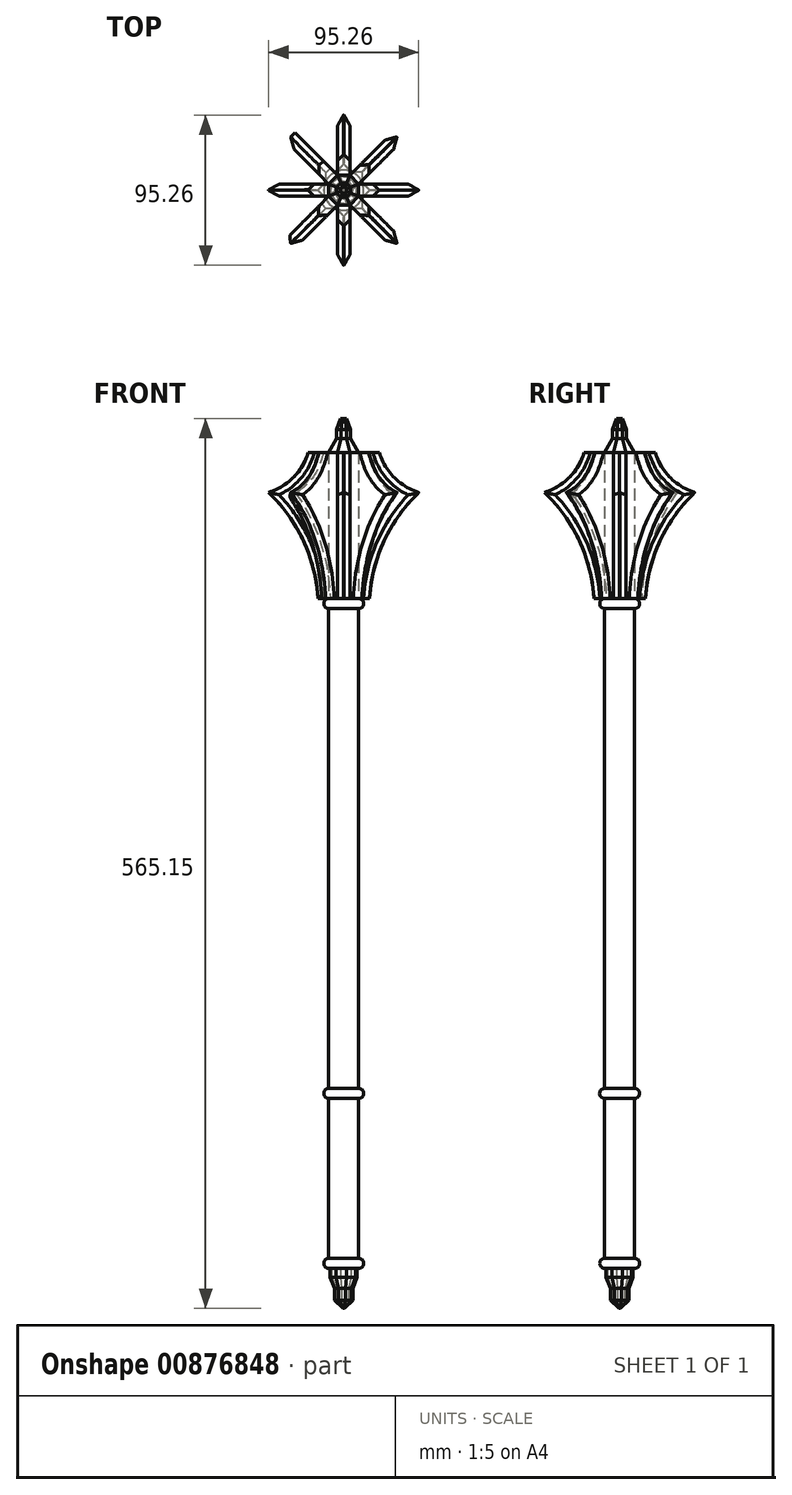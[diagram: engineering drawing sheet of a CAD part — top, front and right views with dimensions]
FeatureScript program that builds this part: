
annotation { "Feature Type Name" : "Feature", "Feature Type Description" : "" }
export const myFeature = defineFeature(function(context is Context, id is Id, definition is map)
    precondition{}
    {
        {
            var Q0;
            Q0=qCreatedBy(makeId("Top.planeOp"),FACE);
            var sketch = newSketch(context, id + "F0", { "sketchPlane" : qUnion([Q0])});
            skCircle(sketch, "E0", {"center": v(0, 0) * mm, "radius": 12.7 * mm});
            skSolve(sketch);
        }
        {
            var Q0;
            Q0 = qSketchRegion(id + "F0", true);
            extrude(context, id + "F1", {"entities" : qUnion([Q0]), "depth" : 6.35 * mm, "offsetDistance" : 25.4 * mm});
        }
        {
            var Q0;
            Q0=makeQuery(id+"F1.opExtrude","CAP_EDGE",EDGE,{"disambiguationData":[OSD([sQuery(id+"F0.wireOp",EDGE,"E0")])],"isStart":false});
            var Q1;
            Q1=makeQuery(id+"F1.opExtrude","CAP_EDGE",EDGE,{"disambiguationData":[OSD([sQuery(id+"F0.wireOp",EDGE,"E0")])],"isStart":true});
            fillet(context, id + "F2", {"entities" : qUnion([Q0, Q1]), "radius" : 3.17 * mm, "tangentPropagation" : true, "allowEdgeOverflow" : false});
        }
        {
            var Q0;
            Q0=makeQuery(id+"F1.opExtrude","CAP_FACE",FACE,{"disambiguationData":[OSD([sQuery(id+"F0.wireOp",EDGE,"E0")])],"isStart":false});
            extrude(context, id + "F3", {"entities" : qUnion([Q0]), "operationType" : NewBodyOperationType.ADD, "depth" : 101.6 * mm, "offsetDistance" : 25.4 * mm});
        }
        {
            var Q0;
            Q0=makeQuery(id+"F3.opExtrude","CAP_FACE",FACE,{"disambiguationData":[OSD([sQuery(id+"F0.wireOp",EDGE,"E0")])],"isStart":false});
            var sketch = newSketch(context, id + "F4", { "sketchPlane" : qUnion([Q0])});
            skCircle(sketch, "E1", {"center": v(0, 0) * mm, "radius": 12.7 * mm});
            skSolve(sketch);
        }
        {
            var Q0;
            Q0 = qSketchRegion(id + "F4", true);
            extrude(context, id + "F5", {"entities" : qUnion([Q0]), "operationType" : NewBodyOperationType.ADD, "depth" : 6.35 * mm, "offsetDistance" : 25.4 * mm});
        }
        {
            var Q0;
            Q0=makeQuery(id+"F5.opExtrude","CAP_EDGE",EDGE,{"disambiguationData":[OSD([sQuery(id+"F4.wireOp",EDGE,"E1")])],"isStart":false});
            var Q1;
            Q1=makeQuery(id+"F5.opExtrude","CAP_EDGE",EDGE,{"disambiguationData":[OSD([sQuery(id+"F4.wireOp",EDGE,"E1")])],"isStart":true});
            fillet(context, id + "F6", {"entities" : qUnion([Q0, Q1]), "radius" : 3.17 * mm, "tangentPropagation" : true, "allowEdgeOverflow" : false});
        }
        {
            var Q0;
            Q0=makeQuery(id+"F1.opExtrude","CAP_FACE",FACE,{"disambiguationData":[OSD([sQuery(id+"F0.wireOp",EDGE,"E0")])],"isStart":true});
            var sketch = newSketch(context, id + "F7", { "sketchPlane" : qUnion([Q0])});
            skCircle(sketch, "E2", {"center": v(0, 0) * mm, "radius": 6.35 * mm});
            skSolve(sketch);
        }
        {
            var Q0;
            Q0=makeQuery(id+"F5.opExtrude","CAP_FACE",FACE,{"disambiguationData":[OSD([sQuery(id+"F4.wireOp",EDGE,"E1")])],"isStart":false});
            extrude(context, id + "F8", {"entities" : qUnion([Q0]), "operationType" : NewBodyOperationType.ADD, "depth" : 304.8 * mm, "offsetDistance" : 25.4 * mm});
        }
        {
            var Q0;
            Q0=makeQuery(id+"F8.opExtrude","CAP_FACE",FACE,{"disambiguationData":[OSD([sQuery(id+"F4.wireOp",EDGE,"E1")])],"isStart":false});
            var sketch = newSketch(context, id + "F9", { "sketchPlane" : qUnion([Q0])});
            skCircle(sketch, "E3", {"center": v(0, 0) * mm, "radius": 12.7 * mm});
            skSolve(sketch);
        }
        {
            var Q0;
            Q0 = qSketchRegion(id + "F9", true);
            extrude(context, id + "F10", {"entities" : qUnion([Q0]), "operationType" : NewBodyOperationType.ADD, "depth" : 6.35 * mm, "offsetDistance" : 25.4 * mm});
        }
        {
            var Q0;
            Q0=makeQuery(id+"F10.opExtrude","CAP_EDGE",EDGE,{"disambiguationData":[OSD([sQuery(id+"F9.wireOp",EDGE,"E3")])],"isStart":false});
            var Q1;
            Q1=makeQuery(id+"F10.opExtrude","CAP_EDGE",EDGE,{"disambiguationData":[OSD([sQuery(id+"F9.wireOp",EDGE,"E3")])],"isStart":true});
            fillet(context, id + "F11", {"entities" : qUnion([Q0, Q1]), "radius" : 3.17 * mm, "tangentPropagation" : true, "allowEdgeOverflow" : false});
        }
        {
            var Q0;
            Q0=makeQuery(id+"F10.opExtrude","CAP_FACE",FACE,{"disambiguationData":[OSD([sQuery(id+"F9.wireOp",EDGE,"E3")])],"isStart":false});
            var sketch = newSketch(context, id + "F12", { "sketchPlane" : qUnion([Q0])});
            skCircle(sketch, "E4.cCircle", {"center": v(0, 0) * mm, "radius": 9.53 * mm, "construction": true});
            skLineSegment(sketch, "E4.0", {"start": v(-3.95, 9.53) * mm, "end": v(3.95, 9.53) * mm});
            skLineSegment(sketch, "E4.1", {"start": v(3.95, 9.53) * mm, "end": v(9.53, 3.95) * mm});
            skLineSegment(sketch, "E4.2", {"start": v(9.53, 3.95) * mm, "end": v(9.53, -3.95) * mm});
            skLineSegment(sketch, "E4.3", {"start": v(9.53, -3.95) * mm, "end": v(3.95, -9.53) * mm});
            skLineSegment(sketch, "E4.4", {"start": v(3.95, -9.53) * mm, "end": v(-3.95, -9.53) * mm});
            skLineSegment(sketch, "E4.5", {"start": v(-3.95, -9.53) * mm, "end": v(-9.52, -3.95) * mm});
            skLineSegment(sketch, "E4.6", {"start": v(-9.52, -3.95) * mm, "end": v(-9.53, 3.95) * mm});
            skLineSegment(sketch, "E4.7", {"start": v(-9.53, 3.95) * mm, "end": v(-3.95, 9.53) * mm});
            skPoint(sketch, "E4.0.midPoint", {"position": v(0, 9.53) * mm});
            skSolve(sketch);
        }
        {
            var Q0;
            Q0 = qSketchRegion(id + "F12", true);
            extrude(context, id + "F13", {"entities" : qUnion([Q0]), "operationType" : NewBodyOperationType.ADD, "depth" : 101.6 * mm, "offsetDistance" : 25.4 * mm});
        }
        {
            var Q0;
            Q0=makeQuery(id+"F13.opExtrude","CAP_EDGE",EDGE,{"disambiguationData":[OSD([sQuery(id+"F12.wireOp",EDGE,"E4.5")])],"isStart":false});
            var Q1;
            Q1=makeQuery(id+"F13.opExtrude","CAP_EDGE",EDGE,{"disambiguationData":[OSD([sQuery(id+"F12.wireOp",EDGE,"E4.6")])],"isStart":false});
            var Q2;
            Q2=makeQuery(id+"F13.opExtrude","CAP_EDGE",EDGE,{"disambiguationData":[OSD([sQuery(id+"F12.wireOp",EDGE,"E4.0")])],"isStart":false});
            var Q3;
            Q3=makeQuery(id+"F13.opExtrude","CAP_EDGE",EDGE,{"disambiguationData":[OSD([sQuery(id+"F12.wireOp",EDGE,"E4.1")])],"isStart":false});
            var Q4;
            Q4=makeQuery(id+"F13.opExtrude","CAP_EDGE",EDGE,{"disambiguationData":[OSD([sQuery(id+"F12.wireOp",EDGE,"E4.2")])],"isStart":false});
            var Q5;
            Q5=makeQuery(id+"F13.opExtrude","CAP_EDGE",EDGE,{"disambiguationData":[OSD([sQuery(id+"F12.wireOp",EDGE,"E4.4")])],"isStart":false});
            var Q6;
            Q6=makeQuery(id+"F13.opExtrude","CAP_EDGE",EDGE,{"disambiguationData":[OSD([sQuery(id+"F12.wireOp",EDGE,"E4.7")])],"isStart":false});
            var Q7;
            Q7=makeQuery(id+"F13.opExtrude","CAP_EDGE",EDGE,{"disambiguationData":[OSD([sQuery(id+"F12.wireOp",EDGE,"E4.3")])],"isStart":false});
            chamfer(context, id + "F14", {"entities" : qUnion([Q0, Q1, Q2, Q3, Q4, Q5, Q6, Q7]), "chamferType" : ChamferType.OFFSET_ANGLE, "width" : 5.08 * mm, "oppositeDirection" : true, "angle" : 60 * degree, "tangentPropagation" : true});
        }
        {
            var Q0;
            Q0=makeQuery(id+"F13.opExtrude","SWEPT_FACE",FACE,{"disambiguationData":[OSD([sQuery(id+"F12.wireOp",EDGE,"E4.6")])]});
            extrude(context, id + "F15", {"entities" : qUnion([Q0]), "operationType" : NewBodyOperationType.ADD, "depth" : 38.1 * mm, "offsetDistance" : 25.4 * mm});
        }
        {
            var Q0;
            Q0=makeQuery(id+"F13.opExtrude","SWEPT_FACE",FACE,{"disambiguationData":[OSD([sQuery(id+"F12.wireOp",EDGE,"E4.5")])]});
            extrude(context, id + "F16", {"entities" : qUnion([Q0]), "operationType" : NewBodyOperationType.ADD, "depth" : 38.1 * mm, "offsetDistance" : 25.4 * mm});
        }
        {
            var Q0;
            Q0=makeQuery(id+"F13.opExtrude","SWEPT_FACE",FACE,{"disambiguationData":[OSD([sQuery(id+"F12.wireOp",EDGE,"E4.4")])]});
            extrude(context, id + "F17", {"entities" : qUnion([Q0]), "operationType" : NewBodyOperationType.ADD, "depth" : 38.1 * mm, "offsetDistance" : 25.4 * mm});
        }
        {
            var Q0;
            Q0=makeQuery(id+"F13.opExtrude","SWEPT_FACE",FACE,{"disambiguationData":[OSD([sQuery(id+"F12.wireOp",EDGE,"E4.7")])]});
            extrude(context, id + "F18", {"entities" : qUnion([Q0]), "operationType" : NewBodyOperationType.ADD, "depth" : 38.1 * mm, "offsetDistance" : 25.4 * mm});
        }
        {
            var Q0;
            Q0=makeQuery(id+"F13.opExtrude","SWEPT_FACE",FACE,{"disambiguationData":[OSD([sQuery(id+"F12.wireOp",EDGE,"E4.0")])]});
            extrude(context, id + "F19", {"entities" : qUnion([Q0]), "operationType" : NewBodyOperationType.ADD, "depth" : 38.1 * mm, "offsetDistance" : 25.4 * mm});
        }
        {
            var Q0;
            Q0=makeQuery(id+"F13.opExtrude","SWEPT_FACE",FACE,{"disambiguationData":[OSD([sQuery(id+"F12.wireOp",EDGE,"E4.1")])]});
            extrude(context, id + "F20", {"entities" : qUnion([Q0]), "operationType" : NewBodyOperationType.ADD, "depth" : 38.1 * mm, "offsetDistance" : 25.4 * mm});
        }
        {
            var Q0;
            Q0=makeQuery(id+"F13.opExtrude","SWEPT_FACE",FACE,{"disambiguationData":[OSD([sQuery(id+"F12.wireOp",EDGE,"E4.2")])]});
            extrude(context, id + "F21", {"entities" : qUnion([Q0]), "operationType" : NewBodyOperationType.ADD, "depth" : 38.1 * mm, "offsetDistance" : 25.4 * mm});
        }
        {
            var Q0;
            Q0=makeQuery(id+"F13.opExtrude","SWEPT_FACE",FACE,{"disambiguationData":[OSD([sQuery(id+"F12.wireOp",EDGE,"E4.3")])]});
            extrude(context, id + "F22", {"entities" : qUnion([Q0]), "operationType" : NewBodyOperationType.ADD, "depth" : 38.1 * mm, "offsetDistance" : 25.4 * mm});
        }
        {
            var Q0;
            Q0=makeQuery(id+"F18.opExtrude","SWEPT_FACE",FACE,{"disambiguationData":[OSD([sQuery(id+"F12.wireOp",EDGE,"E4.0"),sQuery(id+"F12.wireOp",EDGE,"E4.7")])]});
            var sketch = newSketch(context, id + "F23", { "sketchPlane" : qUnion([Q0])});
            skLineSegment(sketch, "E5", {"start": v(9.53, 518.25) * mm, "end": v(22.23, 518.25) * mm});
            skLineSegment(sketch, "E6", {"start": v(9.53, 425.45) * mm, "end": v(15.88, 425.45) * mm});
            skLineSegment(sketch, "E7", {"start": v(47.62, 518.25) * mm, "end": v(47.62, 425.45) * mm});
            skLineSegment(sketch, "E8", {"start": v(47.62, 518.25) * mm, "end": v(47.62, 467.45) * mm});
            skLineSegment(sketch, "E9", {"start": v(47.62, 518.25) * mm, "end": v(47.62, 492.85) * mm});
            skArc(sketch, "E10", {"start": v(22.23, 518.25) * mm, "mid": v(31.74, 502.37) * mm, "end": v(47.62, 492.85) * mm});
            skArc(sketch, "E11", {"start": v(47.62, 492.85) * mm, "mid": v(25.35, 462.17) * mm, "end": v(15.87, 425.45) * mm});
            skSolve(sketch);
        }
        {
            var Q0;
            {var subQ0=sQuery(id+"F23.wireOp",EDGE,"E8");Q0=makeQuery(id+"F23.imprint","IMPRINT",FACE,{"disambiguationData":[TD([[makeQuery(id+"F23.imprint","IMPRINT",EDGE,{"derivedFrom":subQ0}),-1.0]])]});}
            var Q1;
            {var subQ0=sQuery(id+"F23.wireOp",EDGE,"E7");Q1=makeQuery(id+"F23.imprint","IMPRINT",FACE,{"disambiguationData":[TD([[makeQuery(id+"F23.imprint","IMPRINT",EDGE,{"derivedFrom":subQ0}),-1.0]])]});}
            var Q2;
            {var subQ0=sQuery(id+"F23.wireOp",EDGE,"E9");Q2=makeQuery(id+"F23.imprint","IMPRINT",FACE,{"disambiguationData":[TD([[makeQuery(id+"F23.imprint","IMPRINT",EDGE,{"derivedFrom":subQ0}),-1.0]])]});}
            extrude(context, id + "F24", {"entities" : qUnion([Q0, Q1, Q2]), "operationType" : NewBodyOperationType.REMOVE, "oppositeDirection" : true, "depth" : 12.7 * mm, "offsetDistance" : 25.4 * mm});
        }
        {
            var Q0;
            Q0=makeQuery(id+"F13.opExtrude","CAP_FACE",FACE,{"disambiguationData":[OSD([sQuery(id+"F12.wireOp",EDGE,"E4.0"),sQuery(id+"F12.wireOp",EDGE,"E4.1"),sQuery(id+"F12.wireOp",EDGE,"E4.2"),sQuery(id+"F12.wireOp",EDGE,"E4.3"),sQuery(id+"F12.wireOp",EDGE,"E4.4"),sQuery(id+"F12.wireOp",EDGE,"E4.5"),sQuery(id+"F12.wireOp",EDGE,"E4.6"),sQuery(id+"F12.wireOp",EDGE,"E4.7")])],"isStart":false});
            extrude(context, id + "F25", {"entities" : qUnion([Q0]), "operationType" : NewBodyOperationType.ADD, "depth" : 12.7 * mm, "offsetDistance" : 25.4 * mm});
        }
        {
            var Q0;
            {var subQ0=sQuery(id+"F12.wireOp",EDGE,"E4.7");var subQ1=sQuery(id+"F12.wireOp",EDGE,"E4.6");var subQ2=sQuery(id+"F12.wireOp",EDGE,"E4.5");var subQ3=sQuery(id+"F12.wireOp",EDGE,"E4.4");var subQ4=sQuery(id+"F12.wireOp",EDGE,"E4.3");var subQ5=sQuery(id+"F12.wireOp",EDGE,"E4.2");var subQ6=sQuery(id+"F12.wireOp",EDGE,"E4.1");var subQ7=sQuery(id+"F12.wireOp",EDGE,"E4.0");Q0=makeQuery(id+"F25.opExtrude","CAP_EDGE",EDGE,{"disambiguationData":[OSD([subQ7,subQ6,subQ5,subQ4,subQ3,subQ2,subQ1,subQ0]),TDD([makeQuery(id+"F14.opChamfer","BLEND_EDGE",EDGE,{"blendedFrom":[makeQuery(id+"F13.opExtrude","CAP_EDGE",EDGE,{"disambiguationData":[OSD([subQ0])],"isStart":false}),makeQuery(id+"F13.opExtrude","CAP_FACE",FACE,{"disambiguationData":[OSD([subQ7,subQ6,subQ5,subQ4,subQ3,subQ2,subQ1,subQ0])],"isStart":false})],"blendedInto":[makeQuery(id+"F13.opExtrude","CAP_FACE",FACE,{"disambiguationData":[OSD([subQ7,subQ6,subQ5,subQ4,subQ3,subQ2,subQ1,subQ0])],"isStart":false})]})])],"isStart":false});}
            var Q1;
            {var subQ0=sQuery(id+"F12.wireOp",EDGE,"E4.7");var subQ1=sQuery(id+"F12.wireOp",EDGE,"E4.6");var subQ2=sQuery(id+"F12.wireOp",EDGE,"E4.5");var subQ3=sQuery(id+"F12.wireOp",EDGE,"E4.4");var subQ4=sQuery(id+"F12.wireOp",EDGE,"E4.3");var subQ5=sQuery(id+"F12.wireOp",EDGE,"E4.2");var subQ6=sQuery(id+"F12.wireOp",EDGE,"E4.1");var subQ7=sQuery(id+"F12.wireOp",EDGE,"E4.0");Q1=makeQuery(id+"F25.opExtrude","CAP_EDGE",EDGE,{"disambiguationData":[OSD([subQ7,subQ6,subQ5,subQ4,subQ3,subQ2,subQ1,subQ0]),TDD([makeQuery(id+"F14.opChamfer","BLEND_EDGE",EDGE,{"blendedFrom":[makeQuery(id+"F13.opExtrude","CAP_EDGE",EDGE,{"disambiguationData":[OSD([subQ7])],"isStart":false}),makeQuery(id+"F13.opExtrude","CAP_FACE",FACE,{"disambiguationData":[OSD([subQ7,subQ6,subQ5,subQ4,subQ3,subQ2,subQ1,subQ0])],"isStart":false})],"blendedInto":[makeQuery(id+"F13.opExtrude","CAP_FACE",FACE,{"disambiguationData":[OSD([subQ7,subQ6,subQ5,subQ4,subQ3,subQ2,subQ1,subQ0])],"isStart":false})]})])],"isStart":false});}
            var Q2;
            {var subQ0=sQuery(id+"F12.wireOp",EDGE,"E4.7");var subQ1=sQuery(id+"F12.wireOp",EDGE,"E4.6");var subQ2=sQuery(id+"F12.wireOp",EDGE,"E4.5");var subQ3=sQuery(id+"F12.wireOp",EDGE,"E4.4");var subQ4=sQuery(id+"F12.wireOp",EDGE,"E4.3");var subQ5=sQuery(id+"F12.wireOp",EDGE,"E4.2");var subQ6=sQuery(id+"F12.wireOp",EDGE,"E4.1");var subQ7=sQuery(id+"F12.wireOp",EDGE,"E4.0");Q2=makeQuery(id+"F25.opExtrude","CAP_EDGE",EDGE,{"disambiguationData":[OSD([subQ7,subQ6,subQ5,subQ4,subQ3,subQ2,subQ1,subQ0]),TDD([makeQuery(id+"F14.opChamfer","BLEND_EDGE",EDGE,{"blendedFrom":[makeQuery(id+"F13.opExtrude","CAP_EDGE",EDGE,{"disambiguationData":[OSD([subQ6])],"isStart":false}),makeQuery(id+"F13.opExtrude","CAP_FACE",FACE,{"disambiguationData":[OSD([subQ7,subQ6,subQ5,subQ4,subQ3,subQ2,subQ1,subQ0])],"isStart":false})],"blendedInto":[makeQuery(id+"F13.opExtrude","CAP_FACE",FACE,{"disambiguationData":[OSD([subQ7,subQ6,subQ5,subQ4,subQ3,subQ2,subQ1,subQ0])],"isStart":false})]})])],"isStart":false});}
            var Q3;
            {var subQ0=sQuery(id+"F12.wireOp",EDGE,"E4.7");var subQ1=sQuery(id+"F12.wireOp",EDGE,"E4.6");var subQ2=sQuery(id+"F12.wireOp",EDGE,"E4.5");var subQ3=sQuery(id+"F12.wireOp",EDGE,"E4.4");var subQ4=sQuery(id+"F12.wireOp",EDGE,"E4.3");var subQ5=sQuery(id+"F12.wireOp",EDGE,"E4.2");var subQ6=sQuery(id+"F12.wireOp",EDGE,"E4.1");var subQ7=sQuery(id+"F12.wireOp",EDGE,"E4.0");Q3=makeQuery(id+"F25.opExtrude","CAP_EDGE",EDGE,{"disambiguationData":[OSD([subQ7,subQ6,subQ5,subQ4,subQ3,subQ2,subQ1,subQ0]),TDD([makeQuery(id+"F14.opChamfer","BLEND_EDGE",EDGE,{"blendedFrom":[makeQuery(id+"F13.opExtrude","CAP_EDGE",EDGE,{"disambiguationData":[OSD([subQ5])],"isStart":false}),makeQuery(id+"F13.opExtrude","CAP_FACE",FACE,{"disambiguationData":[OSD([subQ7,subQ6,subQ5,subQ4,subQ3,subQ2,subQ1,subQ0])],"isStart":false})],"blendedInto":[makeQuery(id+"F13.opExtrude","CAP_FACE",FACE,{"disambiguationData":[OSD([subQ7,subQ6,subQ5,subQ4,subQ3,subQ2,subQ1,subQ0])],"isStart":false})]})])],"isStart":false});}
            var Q4;
            {var subQ0=sQuery(id+"F12.wireOp",EDGE,"E4.7");var subQ1=sQuery(id+"F12.wireOp",EDGE,"E4.6");var subQ2=sQuery(id+"F12.wireOp",EDGE,"E4.5");var subQ3=sQuery(id+"F12.wireOp",EDGE,"E4.4");var subQ4=sQuery(id+"F12.wireOp",EDGE,"E4.3");var subQ5=sQuery(id+"F12.wireOp",EDGE,"E4.2");var subQ6=sQuery(id+"F12.wireOp",EDGE,"E4.1");var subQ7=sQuery(id+"F12.wireOp",EDGE,"E4.0");Q4=makeQuery(id+"F25.opExtrude","CAP_EDGE",EDGE,{"disambiguationData":[OSD([subQ7,subQ6,subQ5,subQ4,subQ3,subQ2,subQ1,subQ0]),TDD([makeQuery(id+"F14.opChamfer","BLEND_EDGE",EDGE,{"blendedFrom":[makeQuery(id+"F13.opExtrude","CAP_EDGE",EDGE,{"disambiguationData":[OSD([subQ4])],"isStart":false}),makeQuery(id+"F13.opExtrude","CAP_FACE",FACE,{"disambiguationData":[OSD([subQ7,subQ6,subQ5,subQ4,subQ3,subQ2,subQ1,subQ0])],"isStart":false})],"blendedInto":[makeQuery(id+"F13.opExtrude","CAP_FACE",FACE,{"disambiguationData":[OSD([subQ7,subQ6,subQ5,subQ4,subQ3,subQ2,subQ1,subQ0])],"isStart":false})]})])],"isStart":false});}
            var Q5;
            {var subQ0=sQuery(id+"F12.wireOp",EDGE,"E4.7");var subQ1=sQuery(id+"F12.wireOp",EDGE,"E4.6");var subQ2=sQuery(id+"F12.wireOp",EDGE,"E4.5");var subQ3=sQuery(id+"F12.wireOp",EDGE,"E4.4");var subQ4=sQuery(id+"F12.wireOp",EDGE,"E4.3");var subQ5=sQuery(id+"F12.wireOp",EDGE,"E4.2");var subQ6=sQuery(id+"F12.wireOp",EDGE,"E4.1");var subQ7=sQuery(id+"F12.wireOp",EDGE,"E4.0");Q5=makeQuery(id+"F25.opExtrude","CAP_EDGE",EDGE,{"disambiguationData":[OSD([subQ7,subQ6,subQ5,subQ4,subQ3,subQ2,subQ1,subQ0]),TDD([makeQuery(id+"F14.opChamfer","BLEND_EDGE",EDGE,{"blendedFrom":[makeQuery(id+"F13.opExtrude","CAP_EDGE",EDGE,{"disambiguationData":[OSD([subQ3])],"isStart":false}),makeQuery(id+"F13.opExtrude","CAP_FACE",FACE,{"disambiguationData":[OSD([subQ7,subQ6,subQ5,subQ4,subQ3,subQ2,subQ1,subQ0])],"isStart":false})],"blendedInto":[makeQuery(id+"F13.opExtrude","CAP_FACE",FACE,{"disambiguationData":[OSD([subQ7,subQ6,subQ5,subQ4,subQ3,subQ2,subQ1,subQ0])],"isStart":false})]})])],"isStart":false});}
            var Q6;
            {var subQ0=sQuery(id+"F12.wireOp",EDGE,"E4.7");var subQ1=sQuery(id+"F12.wireOp",EDGE,"E4.6");var subQ2=sQuery(id+"F12.wireOp",EDGE,"E4.5");var subQ3=sQuery(id+"F12.wireOp",EDGE,"E4.4");var subQ4=sQuery(id+"F12.wireOp",EDGE,"E4.3");var subQ5=sQuery(id+"F12.wireOp",EDGE,"E4.2");var subQ6=sQuery(id+"F12.wireOp",EDGE,"E4.1");var subQ7=sQuery(id+"F12.wireOp",EDGE,"E4.0");Q6=makeQuery(id+"F25.opExtrude","CAP_EDGE",EDGE,{"disambiguationData":[OSD([subQ7,subQ6,subQ5,subQ4,subQ3,subQ2,subQ1,subQ0]),TDD([makeQuery(id+"F14.opChamfer","BLEND_EDGE",EDGE,{"blendedFrom":[makeQuery(id+"F13.opExtrude","CAP_EDGE",EDGE,{"disambiguationData":[OSD([subQ2])],"isStart":false}),makeQuery(id+"F13.opExtrude","CAP_FACE",FACE,{"disambiguationData":[OSD([subQ7,subQ6,subQ5,subQ4,subQ3,subQ2,subQ1,subQ0])],"isStart":false})],"blendedInto":[makeQuery(id+"F13.opExtrude","CAP_FACE",FACE,{"disambiguationData":[OSD([subQ7,subQ6,subQ5,subQ4,subQ3,subQ2,subQ1,subQ0])],"isStart":false})]})])],"isStart":false});}
            var Q7;
            {var subQ0=sQuery(id+"F12.wireOp",EDGE,"E4.7");var subQ1=sQuery(id+"F12.wireOp",EDGE,"E4.6");var subQ2=sQuery(id+"F12.wireOp",EDGE,"E4.5");var subQ3=sQuery(id+"F12.wireOp",EDGE,"E4.4");var subQ4=sQuery(id+"F12.wireOp",EDGE,"E4.3");var subQ5=sQuery(id+"F12.wireOp",EDGE,"E4.2");var subQ6=sQuery(id+"F12.wireOp",EDGE,"E4.1");var subQ7=sQuery(id+"F12.wireOp",EDGE,"E4.0");Q7=makeQuery(id+"F25.opExtrude","CAP_EDGE",EDGE,{"disambiguationData":[OSD([subQ7,subQ6,subQ5,subQ4,subQ3,subQ2,subQ1,subQ0]),TDD([makeQuery(id+"F14.opChamfer","BLEND_EDGE",EDGE,{"blendedFrom":[makeQuery(id+"F13.opExtrude","CAP_EDGE",EDGE,{"disambiguationData":[OSD([subQ1])],"isStart":false}),makeQuery(id+"F13.opExtrude","CAP_FACE",FACE,{"disambiguationData":[OSD([subQ7,subQ6,subQ5,subQ4,subQ3,subQ2,subQ1,subQ0])],"isStart":false})],"blendedInto":[makeQuery(id+"F13.opExtrude","CAP_FACE",FACE,{"disambiguationData":[OSD([subQ7,subQ6,subQ5,subQ4,subQ3,subQ2,subQ1,subQ0])],"isStart":false})]})])],"isStart":false});}
            chamfer(context, id + "F26", {"entities" : qUnion([Q0, Q1, Q2, Q3, Q4, Q5, Q6, Q7]), "chamferType" : ChamferType.OFFSET_ANGLE, "width" : 2.54 * mm, "oppositeDirection" : false, "angle" : 70 * degree, "tangentPropagation" : true});
        }
        {
            var Q0;
            {var subQ0=sQuery(id+"F23.wireOp",EDGE,"E9");Q0=makeQuery(id+"F23.imprint","IMPRINT",FACE,{"disambiguationData":[TD([[makeQuery(id+"F23.imprint","IMPRINT",EDGE,{"derivedFrom":subQ0}),-1.0]])]});}
            var Q1;
            {var subQ0=sQuery(id+"F23.wireOp",EDGE,"E7");Q1=makeQuery(id+"F23.imprint","IMPRINT",FACE,{"disambiguationData":[TD([[makeQuery(id+"F23.imprint","IMPRINT",EDGE,{"derivedFrom":subQ0}),-1.0]])]});}
            var Q2;
            {var subQ0=sQuery(id+"F0.wireOp",EDGE,"E0");Q2=makeQuery(id+"F2.opFillet","BLEND_EDGE",EDGE,{"blendedFrom":[makeQuery(id+"F1.opExtrude","CAP_EDGE",EDGE,{"disambiguationData":[OSD([subQ0])],"isStart":true}),makeQuery(id+"F1.opExtrude","CAP_FACE",FACE,{"disambiguationData":[OSD([subQ0])],"isStart":true})],"blendedInto":[makeQuery(id+"F1.opExtrude","CAP_FACE",FACE,{"disambiguationData":[OSD([subQ0])],"isStart":true})]});}
            revolve(context, id + "F27", {"operationType" : NewBodyOperationType.REMOVE, "surfaceOperationType" : NewSurfaceOperationType.NEW, "entities" : qUnion([Q0, Q1]), "axis" : qUnion([Q2]), "revolveType" : RevolveType.FULL, "oppositeDirection" : true});
        }
        {
            var Q0;
            Q0=makeQuery(id+"F7.imprint","IMPRINT",FACE,{"disambiguationData":[TD([[makeQuery(id+"F7.imprint","IMPRINT",EDGE,{"derivedFrom":sQuery(id+"F7.wireOp",EDGE,"E2")}),-1.0]])]});
            var sketch = newSketch(context, id + "F28", { "sketchPlane" : qUnion([Q0])});
            skCircle(sketch, "E12.cCircle", {"center": v(0, 0) * mm, "radius": 8.09 * mm, "construction": true});
            skLineSegment(sketch, "E12.0", {"start": v(-7.31, -4.8) * mm, "end": v(-8.57, 1.77) * mm});
            skLineSegment(sketch, "E12.1", {"start": v(-8.57, 1.77) * mm, "end": v(-4.8, 7.31) * mm});
            skLineSegment(sketch, "E12.2", {"start": v(-4.8, 7.31) * mm, "end": v(1.77, 8.57) * mm});
            skLineSegment(sketch, "E12.3", {"start": v(1.77, 8.57) * mm, "end": v(7.31, 4.8) * mm});
            skLineSegment(sketch, "E12.4", {"start": v(7.31, 4.8) * mm, "end": v(8.57, -1.77) * mm});
            skLineSegment(sketch, "E12.5", {"start": v(8.57, -1.77) * mm, "end": v(4.8, -7.31) * mm});
            skLineSegment(sketch, "E12.6", {"start": v(4.8, -7.31) * mm, "end": v(-1.77, -8.57) * mm});
            skLineSegment(sketch, "E12.7", {"start": v(-1.77, -8.57) * mm, "end": v(-7.31, -4.8) * mm});
            skPoint(sketch, "E12.0.midPoint", {"position": v(-7.94, -1.52) * mm});
            skSolve(sketch);
        }
        {
            var Q0;
            Q0 = qSketchRegion(id + "F28", true);
            extrude(context, id + "F29", {"entities" : qUnion([Q0]), "operationType" : NewBodyOperationType.ADD, "depth" : 12.7 * mm, "offsetDistance" : 25.4 * mm});
        }
        {
            var Q0;
            Q0=makeQuery(id+"F29.opExtrude","CAP_EDGE",EDGE,{"disambiguationData":[OSD([sQuery(id+"F28.wireOp",EDGE,"E12.3")])],"isStart":false});
            var Q1;
            Q1=makeQuery(id+"F29.opExtrude","CAP_EDGE",EDGE,{"disambiguationData":[OSD([sQuery(id+"F28.wireOp",EDGE,"E12.4")])],"isStart":false});
            var Q2;
            Q2=makeQuery(id+"F29.opExtrude","CAP_FACE",FACE,{"disambiguationData":[OSD([sQuery(id+"F28.wireOp",EDGE,"E12.0"),sQuery(id+"F28.wireOp",EDGE,"E12.1"),sQuery(id+"F28.wireOp",EDGE,"E12.2"),sQuery(id+"F28.wireOp",EDGE,"E12.3"),sQuery(id+"F28.wireOp",EDGE,"E12.4"),sQuery(id+"F28.wireOp",EDGE,"E12.5"),sQuery(id+"F28.wireOp",EDGE,"E12.6"),sQuery(id+"F28.wireOp",EDGE,"E12.7")])],"isStart":false});
            chamfer(context, id + "F30", {"entities" : qUnion([Q0, Q1, Q2]), "chamferType" : ChamferType.OFFSET_ANGLE, "width" : 2.54 * mm, "oppositeDirection" : true, "angle" : 70 * degree, "tangentPropagation" : true});
        }
        {
            var Q0;
            Q0=makeQuery(id+"F29.opExtrude","CAP_FACE",FACE,{"disambiguationData":[OSD([sQuery(id+"F28.wireOp",EDGE,"E12.0"),sQuery(id+"F28.wireOp",EDGE,"E12.1"),sQuery(id+"F28.wireOp",EDGE,"E12.2"),sQuery(id+"F28.wireOp",EDGE,"E12.3"),sQuery(id+"F28.wireOp",EDGE,"E12.4"),sQuery(id+"F28.wireOp",EDGE,"E12.5"),sQuery(id+"F28.wireOp",EDGE,"E12.6"),sQuery(id+"F28.wireOp",EDGE,"E12.7")])],"isStart":false});
            extrude(context, id + "F31", {"entities" : qUnion([Q0]), "operationType" : NewBodyOperationType.ADD, "depth" : 12.7 * mm, "offsetDistance" : 25.4 * mm});
        }
        {
            var Q0;
            Q0=makeQuery(id+"F31.opExtrude","CAP_FACE",FACE,{"disambiguationData":[OSD([sQuery(id+"F28.wireOp",EDGE,"E12.0"),sQuery(id+"F28.wireOp",EDGE,"E12.1"),sQuery(id+"F28.wireOp",EDGE,"E12.2"),sQuery(id+"F28.wireOp",EDGE,"E12.3"),sQuery(id+"F28.wireOp",EDGE,"E12.4"),sQuery(id+"F28.wireOp",EDGE,"E12.5"),sQuery(id+"F28.wireOp",EDGE,"E12.6"),sQuery(id+"F28.wireOp",EDGE,"E12.7")])],"isStart":false});
            chamfer(context, id + "F32", {"entities" : qUnion([Q0]), "width" : 5.08 * mm, "tangentPropagation" : true});
        }
        {
            var Q0;
            Q0=makeQuery(id+"F27.boolean.opBoolean","INTERSECT",EDGE,{"derivedFrom":[makeQuery(id+"F16.opExtrude","SWEPT_FACE",FACE,{"disambiguationData":[OSD([sQuery(id+"F12.wireOp",EDGE,"E4.4"),sQuery(id+"F12.wireOp",EDGE,"E4.5")])]}),makeQuery(id+"F27.opRevolve","SWEPT_FACE",FACE,{"disambiguationData":[OSD([sQuery(id+"F23.wireOp",EDGE,"E11")])]})]});
            var Q1;
            Q1=makeQuery(id+"F27.boolean.opBoolean","INTERSECT",EDGE,{"derivedFrom":[makeQuery(id+"F16.opExtrude","SWEPT_FACE",FACE,{"disambiguationData":[OSD([sQuery(id+"F12.wireOp",EDGE,"E4.4"),sQuery(id+"F12.wireOp",EDGE,"E4.5")])]}),makeQuery(id+"F27.opRevolve","SWEPT_FACE",FACE,{"disambiguationData":[OSD([sQuery(id+"F23.wireOp",EDGE,"E10")])]})]});
            var Q2;
            Q2=makeQuery(id+"F27.boolean.opBoolean","INTERSECT",EDGE,{"derivedFrom":[makeQuery(id+"F15.opExtrude","SWEPT_FACE",FACE,{"disambiguationData":[OSD([sQuery(id+"F12.wireOp",EDGE,"E4.5"),sQuery(id+"F12.wireOp",EDGE,"E4.6")])]}),makeQuery(id+"F27.opRevolve","SWEPT_FACE",FACE,{"disambiguationData":[OSD([sQuery(id+"F23.wireOp",EDGE,"E10")])]})]});
            var Q3;
            Q3=makeQuery(id+"F27.boolean.opBoolean","INTERSECT",EDGE,{"derivedFrom":[makeQuery(id+"F15.opExtrude","SWEPT_FACE",FACE,{"disambiguationData":[OSD([sQuery(id+"F12.wireOp",EDGE,"E4.6"),sQuery(id+"F12.wireOp",EDGE,"E4.7")])]}),makeQuery(id+"F27.opRevolve","SWEPT_FACE",FACE,{"disambiguationData":[OSD([sQuery(id+"F23.wireOp",EDGE,"E10")])]})]});
            var Q4;
            Q4=makeQuery(id+"F27.boolean.opBoolean","INTERSECT",EDGE,{"derivedFrom":[makeQuery(id+"F15.opExtrude","SWEPT_FACE",FACE,{"disambiguationData":[OSD([sQuery(id+"F12.wireOp",EDGE,"E4.6"),sQuery(id+"F12.wireOp",EDGE,"E4.7")])]}),makeQuery(id+"F27.opRevolve","SWEPT_FACE",FACE,{"disambiguationData":[OSD([sQuery(id+"F23.wireOp",EDGE,"E11")])]})]});
            var Q5;
            Q5=makeQuery(id+"F27.boolean.opBoolean","INTERSECT",EDGE,{"derivedFrom":[makeQuery(id+"F15.opExtrude","SWEPT_FACE",FACE,{"disambiguationData":[OSD([sQuery(id+"F12.wireOp",EDGE,"E4.5"),sQuery(id+"F12.wireOp",EDGE,"E4.6")])]}),makeQuery(id+"F27.opRevolve","SWEPT_FACE",FACE,{"disambiguationData":[OSD([sQuery(id+"F23.wireOp",EDGE,"E11")])]})]});
            var Q6;
            Q6=makeQuery(id+"F24.boolean.opBoolean","INTERSECT",EDGE,{"derivedFrom":[makeQuery(id+"F18.opExtrude","SWEPT_FACE",FACE,{"disambiguationData":[OSD([sQuery(id+"F12.wireOp",EDGE,"E4.6"),sQuery(id+"F12.wireOp",EDGE,"E4.7")])]}),makeQuery(id+"F24.opExtrude","SWEPT_FACE",FACE,{"disambiguationData":[OSD([sQuery(id+"F23.wireOp",EDGE,"E11")])]})]});
            var Q7;
            Q7=makeQuery(id+"F24.boolean.opBoolean","COPY",EDGE,{"derivedFrom":makeQuery(id+"F24.opExtrude","CAP_EDGE",EDGE,{"disambiguationData":[OSD([sQuery(id+"F23.wireOp",EDGE,"E11")])],"isStart":true})});
            var Q8;
            Q8=makeQuery(id+"F27.boolean.opBoolean","INTERSECT",EDGE,{"derivedFrom":[makeQuery(id+"F19.opExtrude","SWEPT_FACE",FACE,{"disambiguationData":[OSD([sQuery(id+"F12.wireOp",EDGE,"E4.0"),sQuery(id+"F12.wireOp",EDGE,"E4.7")])]}),makeQuery(id+"F27.opRevolve","SWEPT_FACE",FACE,{"disambiguationData":[OSD([sQuery(id+"F23.wireOp",EDGE,"E10")])]})]});
            var Q9;
            Q9=makeQuery(id+"F27.boolean.opBoolean","INTERSECT",EDGE,{"derivedFrom":[makeQuery(id+"F19.opExtrude","SWEPT_FACE",FACE,{"disambiguationData":[OSD([sQuery(id+"F12.wireOp",EDGE,"E4.0"),sQuery(id+"F12.wireOp",EDGE,"E4.1")])]}),makeQuery(id+"F27.opRevolve","SWEPT_FACE",FACE,{"disambiguationData":[OSD([sQuery(id+"F23.wireOp",EDGE,"E10")])]})]});
            var Q10;
            Q10=makeQuery(id+"F27.boolean.opBoolean","INTERSECT",EDGE,{"derivedFrom":[makeQuery(id+"F19.opExtrude","SWEPT_FACE",FACE,{"disambiguationData":[OSD([sQuery(id+"F12.wireOp",EDGE,"E4.0"),sQuery(id+"F12.wireOp",EDGE,"E4.1")])]}),makeQuery(id+"F27.opRevolve","SWEPT_FACE",FACE,{"disambiguationData":[OSD([sQuery(id+"F23.wireOp",EDGE,"E11")])]})]});
            var Q11;
            Q11=makeQuery(id+"F27.boolean.opBoolean","INTERSECT",EDGE,{"derivedFrom":[makeQuery(id+"F19.opExtrude","SWEPT_FACE",FACE,{"disambiguationData":[OSD([sQuery(id+"F12.wireOp",EDGE,"E4.0"),sQuery(id+"F12.wireOp",EDGE,"E4.7")])]}),makeQuery(id+"F27.opRevolve","SWEPT_FACE",FACE,{"disambiguationData":[OSD([sQuery(id+"F23.wireOp",EDGE,"E11")])]})]});
            var Q12;
            Q12=makeQuery(id+"F27.boolean.opBoolean","INTERSECT",EDGE,{"derivedFrom":[makeQuery(id+"F20.opExtrude","SWEPT_FACE",FACE,{"disambiguationData":[OSD([sQuery(id+"F12.wireOp",EDGE,"E4.0"),sQuery(id+"F12.wireOp",EDGE,"E4.1")])]}),makeQuery(id+"F27.opRevolve","SWEPT_FACE",FACE,{"disambiguationData":[OSD([sQuery(id+"F23.wireOp",EDGE,"E10")])]})]});
            var Q13;
            Q13=makeQuery(id+"F27.boolean.opBoolean","INTERSECT",EDGE,{"derivedFrom":[makeQuery(id+"F20.opExtrude","SWEPT_FACE",FACE,{"disambiguationData":[OSD([sQuery(id+"F12.wireOp",EDGE,"E4.1"),sQuery(id+"F12.wireOp",EDGE,"E4.2")])]}),makeQuery(id+"F27.opRevolve","SWEPT_FACE",FACE,{"disambiguationData":[OSD([sQuery(id+"F23.wireOp",EDGE,"E10")])]})]});
            var Q14;
            Q14=makeQuery(id+"F27.boolean.opBoolean","INTERSECT",EDGE,{"derivedFrom":[makeQuery(id+"F20.opExtrude","SWEPT_FACE",FACE,{"disambiguationData":[OSD([sQuery(id+"F12.wireOp",EDGE,"E4.0"),sQuery(id+"F12.wireOp",EDGE,"E4.1")])]}),makeQuery(id+"F27.opRevolve","SWEPT_FACE",FACE,{"disambiguationData":[OSD([sQuery(id+"F23.wireOp",EDGE,"E11")])]})]});
            var Q15;
            Q15=makeQuery(id+"F27.boolean.opBoolean","INTERSECT",EDGE,{"derivedFrom":[makeQuery(id+"F20.opExtrude","SWEPT_FACE",FACE,{"disambiguationData":[OSD([sQuery(id+"F12.wireOp",EDGE,"E4.1"),sQuery(id+"F12.wireOp",EDGE,"E4.2")])]}),makeQuery(id+"F27.opRevolve","SWEPT_FACE",FACE,{"disambiguationData":[OSD([sQuery(id+"F23.wireOp",EDGE,"E11")])]})]});
            var Q16;
            Q16=makeQuery(id+"F27.boolean.opBoolean","INTERSECT",EDGE,{"derivedFrom":[makeQuery(id+"F21.opExtrude","SWEPT_FACE",FACE,{"disambiguationData":[OSD([sQuery(id+"F12.wireOp",EDGE,"E4.1"),sQuery(id+"F12.wireOp",EDGE,"E4.2")])]}),makeQuery(id+"F27.opRevolve","SWEPT_FACE",FACE,{"disambiguationData":[OSD([sQuery(id+"F23.wireOp",EDGE,"E11")])]})]});
            var Q17;
            Q17=makeQuery(id+"F27.boolean.opBoolean","INTERSECT",EDGE,{"derivedFrom":[makeQuery(id+"F21.opExtrude","SWEPT_FACE",FACE,{"disambiguationData":[OSD([sQuery(id+"F12.wireOp",EDGE,"E4.2"),sQuery(id+"F12.wireOp",EDGE,"E4.3")])]}),makeQuery(id+"F27.opRevolve","SWEPT_FACE",FACE,{"disambiguationData":[OSD([sQuery(id+"F23.wireOp",EDGE,"E11")])]})]});
            var Q18;
            Q18=makeQuery(id+"F27.boolean.opBoolean","INTERSECT",EDGE,{"derivedFrom":[makeQuery(id+"F22.opExtrude","SWEPT_FACE",FACE,{"disambiguationData":[OSD([sQuery(id+"F12.wireOp",EDGE,"E4.2"),sQuery(id+"F12.wireOp",EDGE,"E4.3")])]}),makeQuery(id+"F27.opRevolve","SWEPT_FACE",FACE,{"disambiguationData":[OSD([sQuery(id+"F23.wireOp",EDGE,"E10")])]})]});
            var Q19;
            Q19=makeQuery(id+"F27.boolean.opBoolean","INTERSECT",EDGE,{"derivedFrom":[makeQuery(id+"F22.opExtrude","SWEPT_FACE",FACE,{"disambiguationData":[OSD([sQuery(id+"F12.wireOp",EDGE,"E4.3"),sQuery(id+"F12.wireOp",EDGE,"E4.4")])]}),makeQuery(id+"F27.opRevolve","SWEPT_FACE",FACE,{"disambiguationData":[OSD([sQuery(id+"F23.wireOp",EDGE,"E10")])]})]});
            var Q20;
            Q20=makeQuery(id+"F27.boolean.opBoolean","INTERSECT",EDGE,{"derivedFrom":[makeQuery(id+"F22.opExtrude","SWEPT_FACE",FACE,{"disambiguationData":[OSD([sQuery(id+"F12.wireOp",EDGE,"E4.2"),sQuery(id+"F12.wireOp",EDGE,"E4.3")])]}),makeQuery(id+"F27.opRevolve","SWEPT_FACE",FACE,{"disambiguationData":[OSD([sQuery(id+"F23.wireOp",EDGE,"E11")])]})]});
            var Q21;
            Q21=makeQuery(id+"F27.boolean.opBoolean","INTERSECT",EDGE,{"derivedFrom":[makeQuery(id+"F22.opExtrude","SWEPT_FACE",FACE,{"disambiguationData":[OSD([sQuery(id+"F12.wireOp",EDGE,"E4.3"),sQuery(id+"F12.wireOp",EDGE,"E4.4")])]}),makeQuery(id+"F27.opRevolve","SWEPT_FACE",FACE,{"disambiguationData":[OSD([sQuery(id+"F23.wireOp",EDGE,"E11")])]})]});
            var Q22;
            Q22=makeQuery(id+"F27.boolean.opBoolean","INTERSECT",EDGE,{"derivedFrom":[makeQuery(id+"F17.opExtrude","SWEPT_FACE",FACE,{"disambiguationData":[OSD([sQuery(id+"F12.wireOp",EDGE,"E4.3"),sQuery(id+"F12.wireOp",EDGE,"E4.4")])]}),makeQuery(id+"F27.opRevolve","SWEPT_FACE",FACE,{"disambiguationData":[OSD([sQuery(id+"F23.wireOp",EDGE,"E10")])]})]});
            var Q23;
            Q23=makeQuery(id+"F27.boolean.opBoolean","INTERSECT",EDGE,{"derivedFrom":[makeQuery(id+"F17.opExtrude","SWEPT_FACE",FACE,{"disambiguationData":[OSD([sQuery(id+"F12.wireOp",EDGE,"E4.4"),sQuery(id+"F12.wireOp",EDGE,"E4.5")])]}),makeQuery(id+"F27.opRevolve","SWEPT_FACE",FACE,{"disambiguationData":[OSD([sQuery(id+"F23.wireOp",EDGE,"E10")])]})]});
            var Q24;
            Q24=makeQuery(id+"F27.boolean.opBoolean","INTERSECT",EDGE,{"derivedFrom":[makeQuery(id+"F17.opExtrude","SWEPT_FACE",FACE,{"disambiguationData":[OSD([sQuery(id+"F12.wireOp",EDGE,"E4.3"),sQuery(id+"F12.wireOp",EDGE,"E4.4")])]}),makeQuery(id+"F27.opRevolve","SWEPT_FACE",FACE,{"disambiguationData":[OSD([sQuery(id+"F23.wireOp",EDGE,"E11")])]})]});
            var Q25;
            Q25=makeQuery(id+"F27.boolean.opBoolean","INTERSECT",EDGE,{"derivedFrom":[makeQuery(id+"F17.opExtrude","SWEPT_FACE",FACE,{"disambiguationData":[OSD([sQuery(id+"F12.wireOp",EDGE,"E4.4"),sQuery(id+"F12.wireOp",EDGE,"E4.5")])]}),makeQuery(id+"F27.opRevolve","SWEPT_FACE",FACE,{"disambiguationData":[OSD([sQuery(id+"F23.wireOp",EDGE,"E11")])]})]});
            chamfer(context, id + "F33", {"entities" : qUnion([Q0, Q1, Q2, Q3, Q4, Q5, Q6, Q7, Q8, Q9, Q10, Q11, Q12, Q13, Q14, Q15, Q16, Q17, Q18, Q19, Q20, Q21, Q22, Q23, Q24, Q25]), "width" : 3.8 * mm, "tangentPropagation" : true});
        }
        {
            var Q0;
            Q0=makeQuery(id+"F24.boolean.opBoolean","COPY",EDGE,{"derivedFrom":makeQuery(id+"F24.opExtrude","CAP_EDGE",EDGE,{"disambiguationData":[OSD([sQuery(id+"F23.wireOp",EDGE,"E10")])],"isStart":true})});
            var Q1;
            Q1=makeQuery(id+"F24.boolean.opBoolean","INTERSECT",EDGE,{"derivedFrom":[makeQuery(id+"F18.opExtrude","SWEPT_FACE",FACE,{"disambiguationData":[OSD([sQuery(id+"F12.wireOp",EDGE,"E4.6"),sQuery(id+"F12.wireOp",EDGE,"E4.7")])]}),makeQuery(id+"F24.opExtrude","SWEPT_FACE",FACE,{"disambiguationData":[OSD([sQuery(id+"F23.wireOp",EDGE,"E10")])]})]});
            var Q2;
            Q2=makeQuery(id+"F27.boolean.opBoolean","INTERSECT",EDGE,{"derivedFrom":[makeQuery(id+"F21.opExtrude","SWEPT_FACE",FACE,{"disambiguationData":[OSD([sQuery(id+"F12.wireOp",EDGE,"E4.2"),sQuery(id+"F12.wireOp",EDGE,"E4.3")])]}),makeQuery(id+"F27.opRevolve","SWEPT_FACE",FACE,{"disambiguationData":[OSD([sQuery(id+"F23.wireOp",EDGE,"E10")])]})]});
            var Q3;
            Q3=makeQuery(id+"F27.boolean.opBoolean","INTERSECT",EDGE,{"derivedFrom":[makeQuery(id+"F21.opExtrude","SWEPT_FACE",FACE,{"disambiguationData":[OSD([sQuery(id+"F12.wireOp",EDGE,"E4.1"),sQuery(id+"F12.wireOp",EDGE,"E4.2")])]}),makeQuery(id+"F27.opRevolve","SWEPT_FACE",FACE,{"disambiguationData":[OSD([sQuery(id+"F23.wireOp",EDGE,"E10")])]})]});
            var Q4;
            Q4=makeQuery(id+"F27.boolean.opBoolean","INTERSECT",EDGE,{"derivedFrom":[makeQuery(id+"F16.opExtrude","SWEPT_FACE",FACE,{"disambiguationData":[OSD([sQuery(id+"F12.wireOp",EDGE,"E4.5"),sQuery(id+"F12.wireOp",EDGE,"E4.6")])]}),makeQuery(id+"F27.opRevolve","SWEPT_FACE",FACE,{"disambiguationData":[OSD([sQuery(id+"F23.wireOp",EDGE,"E10")])]})]});
            chamfer(context, id + "F34", {"entities" : qUnion([Q0, Q1, Q2, Q3, Q4]), "width" : 3.95 * mm, "tangentPropagation" : true});
        }
    });
